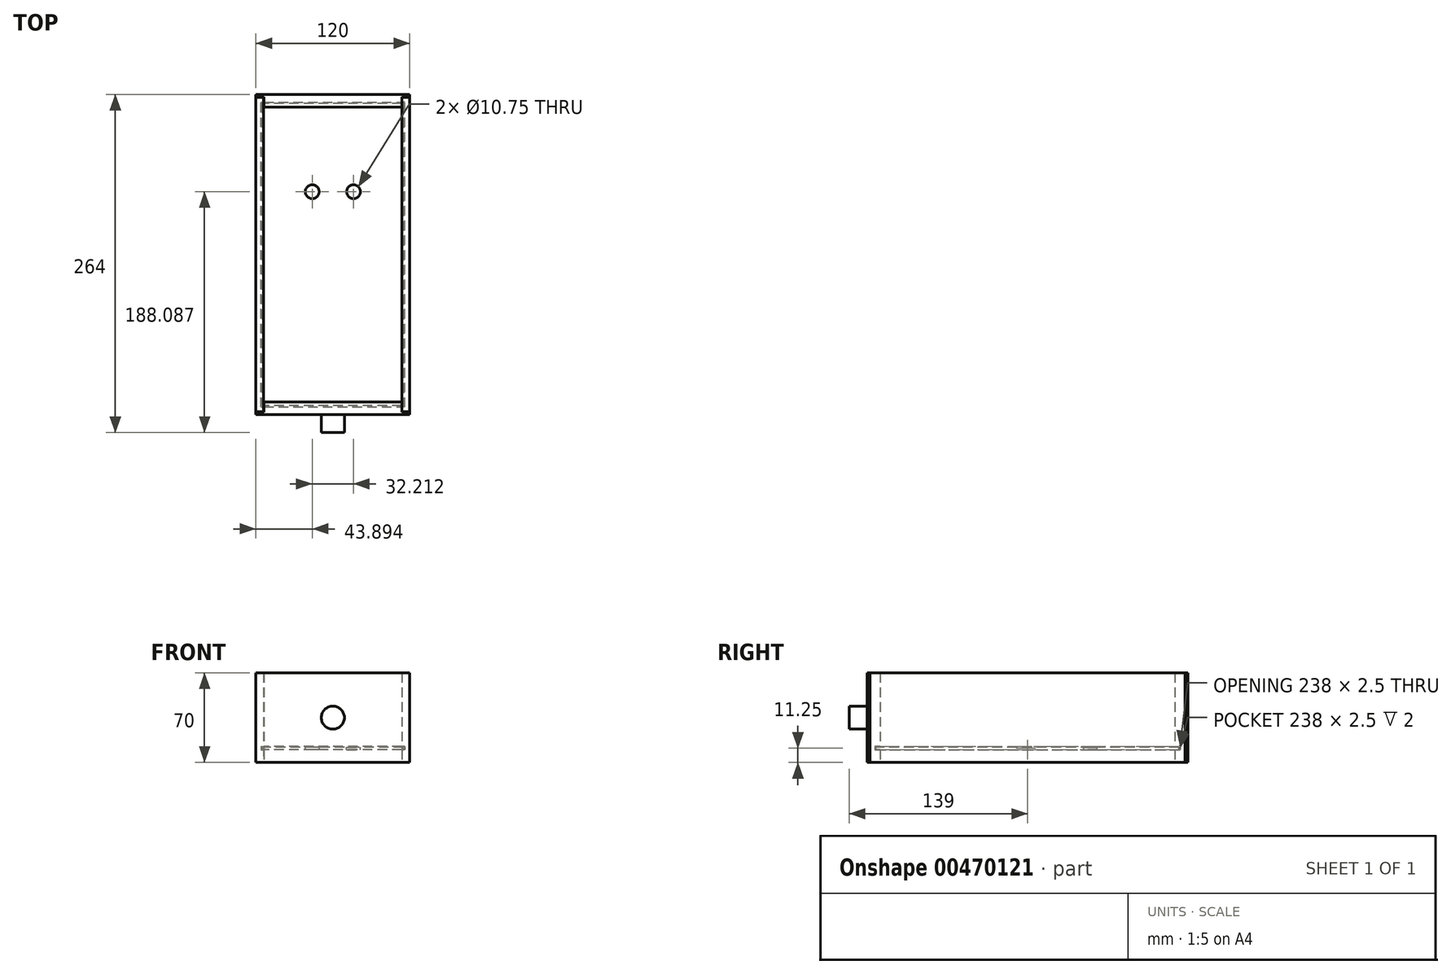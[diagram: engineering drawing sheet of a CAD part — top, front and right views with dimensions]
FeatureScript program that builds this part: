
annotation { "Feature Type Name" : "Feature", "Feature Type Description" : "" }
export const myFeature = defineFeature(function(context is Context, id is Id, definition is map)
    precondition{}
    {
        {
            var Q0;
            Q0=qCreatedBy(makeId("Top.planeOp"),FACE);
            var sketch = newSketch(context, id + "F0", { "sketchPlane" : qUnion([Q0])});
            skLineSegment(sketch, "E0", {"start": v(0, 250) * mm, "end": v(-60, 250) * mm});
            skLineSegment(sketch, "E1", {"start": v(-60, 250) * mm, "end": v(-60, 248) * mm});
            skLineSegment(sketch, "E2", {"start": v(-60, 248) * mm, "end": v(-53.8, 248) * mm});
            skLineSegment(sketch, "E3", {"start": v(-53.8, 248) * mm, "end": v(-53.8, 240) * mm});
            skLineSegment(sketch, "E4", {"start": v(-53.8, 240) * mm, "end": v(0, 240) * mm});
            skLineSegment(sketch, "E5", {"start": v(0, 240) * mm, "end": v(0, 250) * mm});
            skLineSegment(sketch, "E6", {"start": v(0, 0) * mm, "end": v(-60, 0) * mm});
            skLineSegment(sketch, "E7", {"start": v(-60, 0) * mm, "end": v(-60, 2) * mm});
            skLineSegment(sketch, "E8", {"start": v(-60, 2) * mm, "end": v(-53.8, 2) * mm});
            skLineSegment(sketch, "E9", {"start": v(-53.8, 2) * mm, "end": v(-53.8, 10) * mm});
            skLineSegment(sketch, "E10", {"start": v(-53.8, 10) * mm, "end": v(0, 10) * mm});
            skLineSegment(sketch, "E11", {"start": v(0, 10) * mm, "end": v(0, 0) * mm});
            skLineSegment(sketch, "E12.bottom", {"start": v(-60, 247.8) * mm, "end": v(-54, 247.8) * mm});
            skLineSegment(sketch, "E12.top", {"start": v(-60, 2.2) * mm, "end": v(-54, 2.2) * mm});
            skLineSegment(sketch, "E12.left", {"start": v(-60, 247.8) * mm, "end": v(-60, 2.2) * mm});
            skLineSegment(sketch, "E12.right", {"start": v(-54, 247.8) * mm, "end": v(-54, 2.2) * mm});
            skSolve(sketch);
        }
        {
            var Q0;
            Q0 = qSketchRegion(id + "F0", true);
            extrude(context, id + "F1", {"entities" : qUnion([Q0]), "depth" : 70 * mm});
        }
        {
            var Q0;
            Q0=qCreatedBy(makeId("Front.planeOp"),FACE);
            var sketch = newSketch(context, id + "F2", { "sketchPlane" : qUnion([Q0])});
            skArc(sketch, "E13", {"start": v(0, 44) * mm, "mid": v(-9, 35) * mm, "end": v(0, 26) * mm});
            skLineSegment(sketch, "E14", {"start": v(0, 44) * mm, "end": v(0, 26) * mm});
            skSolve(sketch);
        }
        {
            var Q0;
            Q0 = qSketchRegion(id + "F2", true);
            extrude(context, id + "F3", {"entities" : qUnion([Q0]), "depth" : 14 * mm});
        }
        {
            var Q0;
            Q0=qCreatedBy(makeId("Top.planeOp"),FACE);
            cPlane(context, id + "F4", {"entities" : qUnion([Q0]), "cplaneType" : CPlaneType.OFFSET, "offset" : 12 * mm, "width" : 150 * mm, "height" : 150 * mm});
        }
        {
            var Q0;
            Q0=qCreatedBy(makeId("Right.planeOp"),FACE);
            var sketch = newSketch(context, id + "F5", { "sketchPlane" : qUnion([Q0])});
            skLineSegment(sketch, "E15.bottom", {"start": v(6, 12.5) * mm, "end": v(244, 12.5) * mm});
            skLineSegment(sketch, "E15.top", {"start": v(6, 10) * mm, "end": v(244, 10) * mm});
            skLineSegment(sketch, "E15.left", {"start": v(6, 12.5) * mm, "end": v(6, 10) * mm});
            skLineSegment(sketch, "E15.right", {"start": v(244, 12.5) * mm, "end": v(244, 10) * mm});
            skSolve(sketch);
        }
        {
            var Q0;
            Q0 = qSketchRegion(id + "F5", true);
            extrude(context, id + "F6", {"entities" : qUnion([Q0]), "operationType" : NewBodyOperationType.REMOVE, "oppositeDirection" : true, "depth" : 56 * mm});
        }
        {
            var Q0;
            Q0=qCreatedBy(id+"F4.planeOp",FACE);
            var sketch = newSketch(context, id + "F7", { "sketchPlane" : qUnion([Q0])});
            skLineSegment(sketch, "E16.bottom", {"start": v(0, 243) * mm, "end": v(-55, 243) * mm});
            skLineSegment(sketch, "E16.top", {"start": v(0, 7) * mm, "end": v(-55, 7) * mm});
            skLineSegment(sketch, "E16.left", {"start": v(0, 243) * mm, "end": v(0, 7) * mm});
            skLineSegment(sketch, "E16.right", {"start": v(-55, 243) * mm, "end": v(-55, 7) * mm});
            skCircle(sketch, "E17", {"center": v(-16.1, 174.09) * mm, "radius": 5.38 * mm});
            skSolve(sketch);
        }
        {
            var Q0;
            Q0=makeQuery(id+"F7.imprint","IMPRINT",FACE,{"disambiguationData":[TD([[makeQuery(id+"F7.imprint","IMPRINT",EDGE,{"derivedFrom":sQuery(id+"F7.wireOp",EDGE,"E16.bottom")}),1.0]])]});
            var Q1;
            Q1=makeQuery(id+"F6.boolean.opBoolean","INTERSECT",VERTEX,{"derivedFrom":[makeQuery(id+"F1.opExtrude","SWEPT_FACE",FACE,{"disambiguationData":[OSD([sQuery(id+"F0.wireOp",EDGE,"E4")])]}),makeQuery(id+"F6.opExtrude","SWEPT_FACE",FACE,{"disambiguationData":[OSD([sQuery(id+"F5.wireOp",EDGE,"E15.top")])]})]});
            extrude(context, id + "F8", {"entities" : qUnion([Q0]), "oppositeDirection" : true, "endBoundEntityVertex" : qUnion([Q1]), "depth" : 2 * mm});
        }
        {
            var Q0;
            Q0=makeQuery(id+"F1.opExtrude","SWEPT_BODY",BODY,{"disambiguationData":[OSD([sQuery(id+"F0.wireOp",EDGE,"E12.bottom"),sQuery(id+"F0.wireOp",EDGE,"E12.top"),sQuery(id+"F0.wireOp",EDGE,"E12.left"),sQuery(id+"F0.wireOp",EDGE,"E12.right")])]});
            var Q1;
            Q1=makeQuery(id+"F1.opExtrude","SWEPT_BODY",BODY,{"disambiguationData":[OSD([sQuery(id+"F0.wireOp",EDGE,"E6"),sQuery(id+"F0.wireOp",EDGE,"E7"),sQuery(id+"F0.wireOp",EDGE,"E8"),sQuery(id+"F0.wireOp",EDGE,"E9"),sQuery(id+"F0.wireOp",EDGE,"E10"),sQuery(id+"F0.wireOp",EDGE,"E11")])]});
            var Q2;
            Q2=makeQuery(id+"F1.opExtrude","SWEPT_BODY",BODY,{"disambiguationData":[OSD([sQuery(id+"F0.wireOp",EDGE,"E0"),sQuery(id+"F0.wireOp",EDGE,"E1"),sQuery(id+"F0.wireOp",EDGE,"E2"),sQuery(id+"F0.wireOp",EDGE,"E3"),sQuery(id+"F0.wireOp",EDGE,"E4"),sQuery(id+"F0.wireOp",EDGE,"E5")])]});
            var Q3;
            Q3=qCreatedBy(makeId("Right.planeOp"),FACE);
            mirror(context, id + "F9", {"operationType" : NewBodyOperationType.ADD, "entities" : qUnion([Q0, Q1, Q2]), "mirrorPlane" : qUnion([Q3])});
        }
        {
            var Q0;
            Q0=makeQuery(id+"F8.opExtrude","SWEPT_BODY",BODY,{"disambiguationData":[OSD([sQuery(id+"F7.wireOp",EDGE,"E16.bottom"),sQuery(id+"F7.wireOp",EDGE,"E16.top"),sQuery(id+"F7.wireOp",EDGE,"E16.left"),sQuery(id+"F7.wireOp",EDGE,"E16.right"),sQuery(id+"F7.wireOp",EDGE,"E17")])]});
            var Q1;
            Q1=makeQuery(id+"F3.opExtrude","SWEPT_BODY",BODY,{"disambiguationData":[OSD([sQuery(id+"F2.wireOp",EDGE,"E13"),sQuery(id+"F2.wireOp",EDGE,"E14")])]});
            var Q2;
            Q2=qCreatedBy(makeId("Right.planeOp"),FACE);
            mirror(context, id + "F10", {"operationType" : NewBodyOperationType.ADD, "entities" : qUnion([Q0, Q1]), "mirrorPlane" : qUnion([Q2])});
        }
    });
